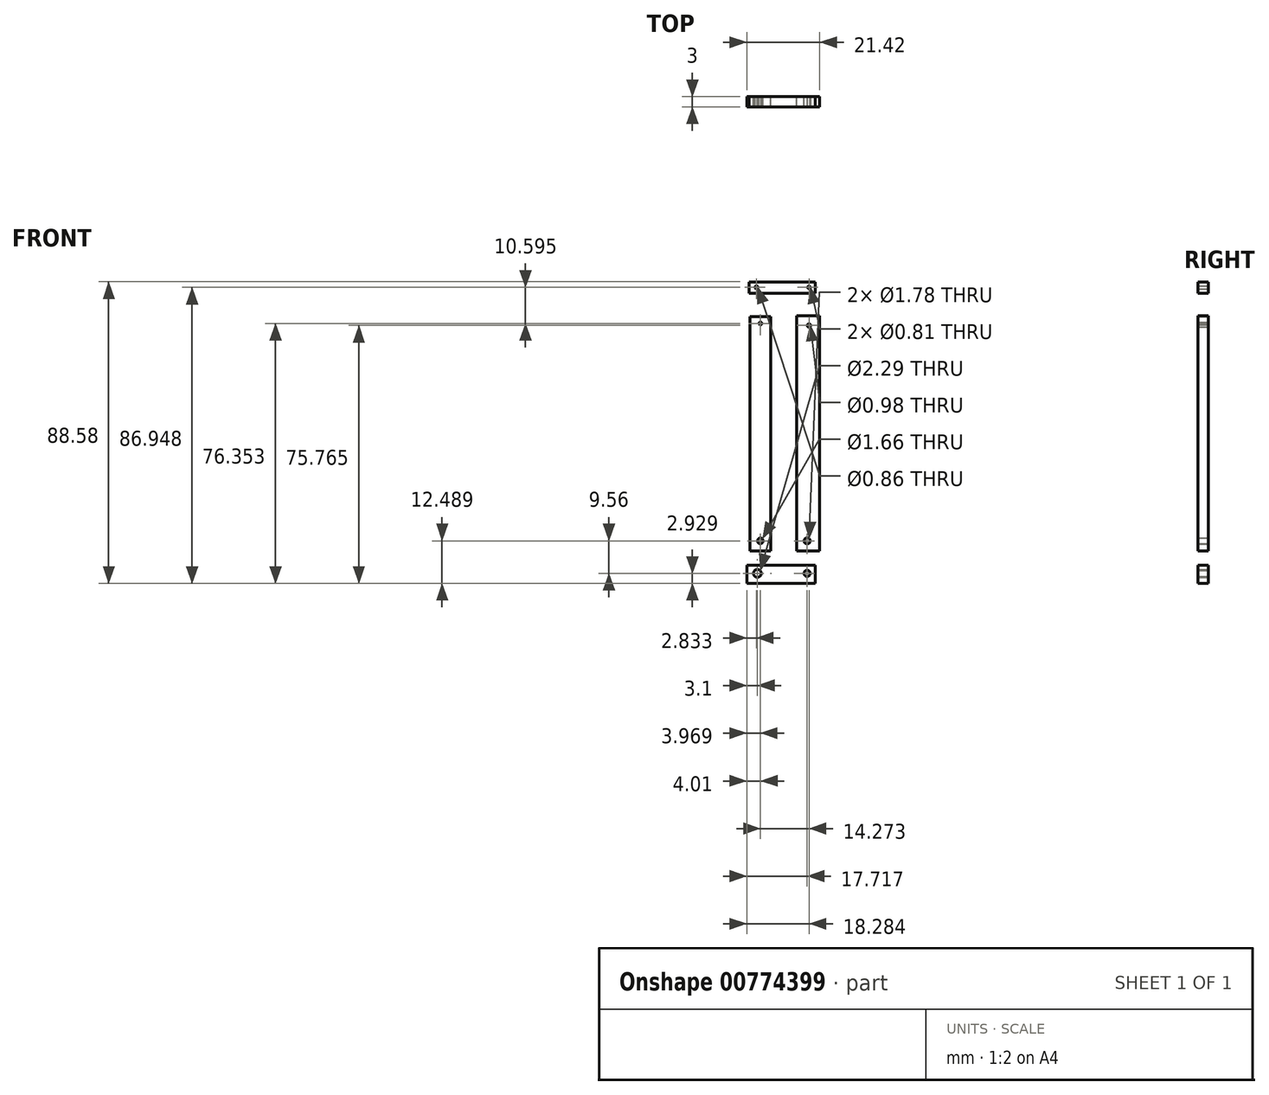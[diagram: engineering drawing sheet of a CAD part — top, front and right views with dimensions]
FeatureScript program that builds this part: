
annotation { "Feature Type Name" : "Feature", "Feature Type Description" : "" }
export const myFeature = defineFeature(function(context is Context, id is Id, definition is map)
    precondition{}
    {
        {
            var Q0;
            Q0=qCreatedBy(makeId("Front.planeOp"),FACE);
            var sketch = newSketch(context, id + "F0", { "sketchPlane" : qUnion([Q0])});
            skLineSegment(sketch, "E0.bottom", {"start": v(-62.46, 41.7) * mm, "end": v(-56.27, 41.7) * mm});
            skLineSegment(sketch, "E0.top", {"start": v(-62.46, -27.23) * mm, "end": v(-56.27, -27.23) * mm});
            skLineSegment(sketch, "E0.left", {"start": v(-62.46, 41.7) * mm, "end": v(-62.46, -27.23) * mm});
            skLineSegment(sketch, "E0.right", {"start": v(-56.27, 41.7) * mm, "end": v(-56.27, -27.23) * mm});
            skLineSegment(sketch, "E1.bottom", {"start": v(-48.76, 41.92) * mm, "end": v(-41.92, 41.92) * mm});
            skLineSegment(sketch, "E1.top", {"start": v(-48.76, -27.23) * mm, "end": v(-41.92, -27.23) * mm});
            skLineSegment(sketch, "E1.left", {"start": v(-48.76, 41.92) * mm, "end": v(-48.76, -27.23) * mm});
            skLineSegment(sketch, "E1.right", {"start": v(-41.92, 41.92) * mm, "end": v(-41.92, -27.23) * mm});
            skLineSegment(sketch, "E2.bottom", {"start": v(-62.68, 51.86) * mm, "end": v(-43.24, 51.86) * mm});
            skLineSegment(sketch, "E2.top", {"start": v(-62.68, 48.54) * mm, "end": v(-43.24, 48.54) * mm});
            skLineSegment(sketch, "E2.left", {"start": v(-62.68, 51.86) * mm, "end": v(-62.68, 48.54) * mm});
            skLineSegment(sketch, "E2.right", {"start": v(-43.24, 51.86) * mm, "end": v(-43.24, 48.54) * mm});
            skLineSegment(sketch, "E3.bottom", {"start": v(-63.34, -31.42) * mm, "end": v(-43.24, -31.42) * mm});
            skLineSegment(sketch, "E3.top", {"start": v(-63.34, -36.72) * mm, "end": v(-43.24, -36.72) * mm});
            skLineSegment(sketch, "E3.left", {"start": v(-63.34, -31.42) * mm, "end": v(-63.34, -36.72) * mm});
            skLineSegment(sketch, "E3.right", {"start": v(-43.24, -31.42) * mm, "end": v(-43.24, -36.72) * mm});
            skPoint(sketch, "E4", {"position": v(-60.5, 50.23) * mm});
            skPoint(sketch, "E5", {"position": v(-45.06, 50.23) * mm});
            skPoint(sketch, "E6", {"position": v(-59.33, 39.63) * mm});
            skPoint(sketch, "E7", {"position": v(-45.06, 39.04) * mm});
            skPoint(sketch, "E8", {"position": v(-60.24, -33.8) * mm});
            skPoint(sketch, "E9", {"position": v(-45.62, -33.8) * mm});
            skPoint(sketch, "E10", {"position": v(-59.37, -24.23) * mm});
            skPoint(sketch, "E11", {"position": v(-45.62, -24.23) * mm});
            skCircle(sketch, "E12", {"center": v(-60.5, 50.23) * mm, "radius": 0.43 * mm});
            skCircle(sketch, "E13", {"center": v(-45.06, 50.23) * mm, "radius": 0.4 * mm});
            skCircle(sketch, "E14", {"center": v(-59.33, 39.63) * mm, "radius": 0.4 * mm});
            skCircle(sketch, "E15", {"center": v(-45.06, 39.04) * mm, "radius": 0.5 * mm});
            skCircle(sketch, "E16", {"center": v(-59.37, -24.23) * mm, "radius": 0.83 * mm});
            skCircle(sketch, "E17", {"center": v(-45.62, -24.23) * mm, "radius": 0.89 * mm});
            skCircle(sketch, "E18", {"center": v(-60.24, -33.8) * mm, "radius": 1.14 * mm});
            skCircle(sketch, "E19", {"center": v(-45.62, -33.8) * mm, "radius": 0.9 * mm});
            skSolve(sketch);
        }
        {
            var Q0;
            Q0 = qSketchRegion(id + "F0", true);
            extrude(context, id + "F1", {"entities" : qUnion([Q0]), "depth" : 3 * mm, "offsetDistance" : 25 * mm});
        }
    });
